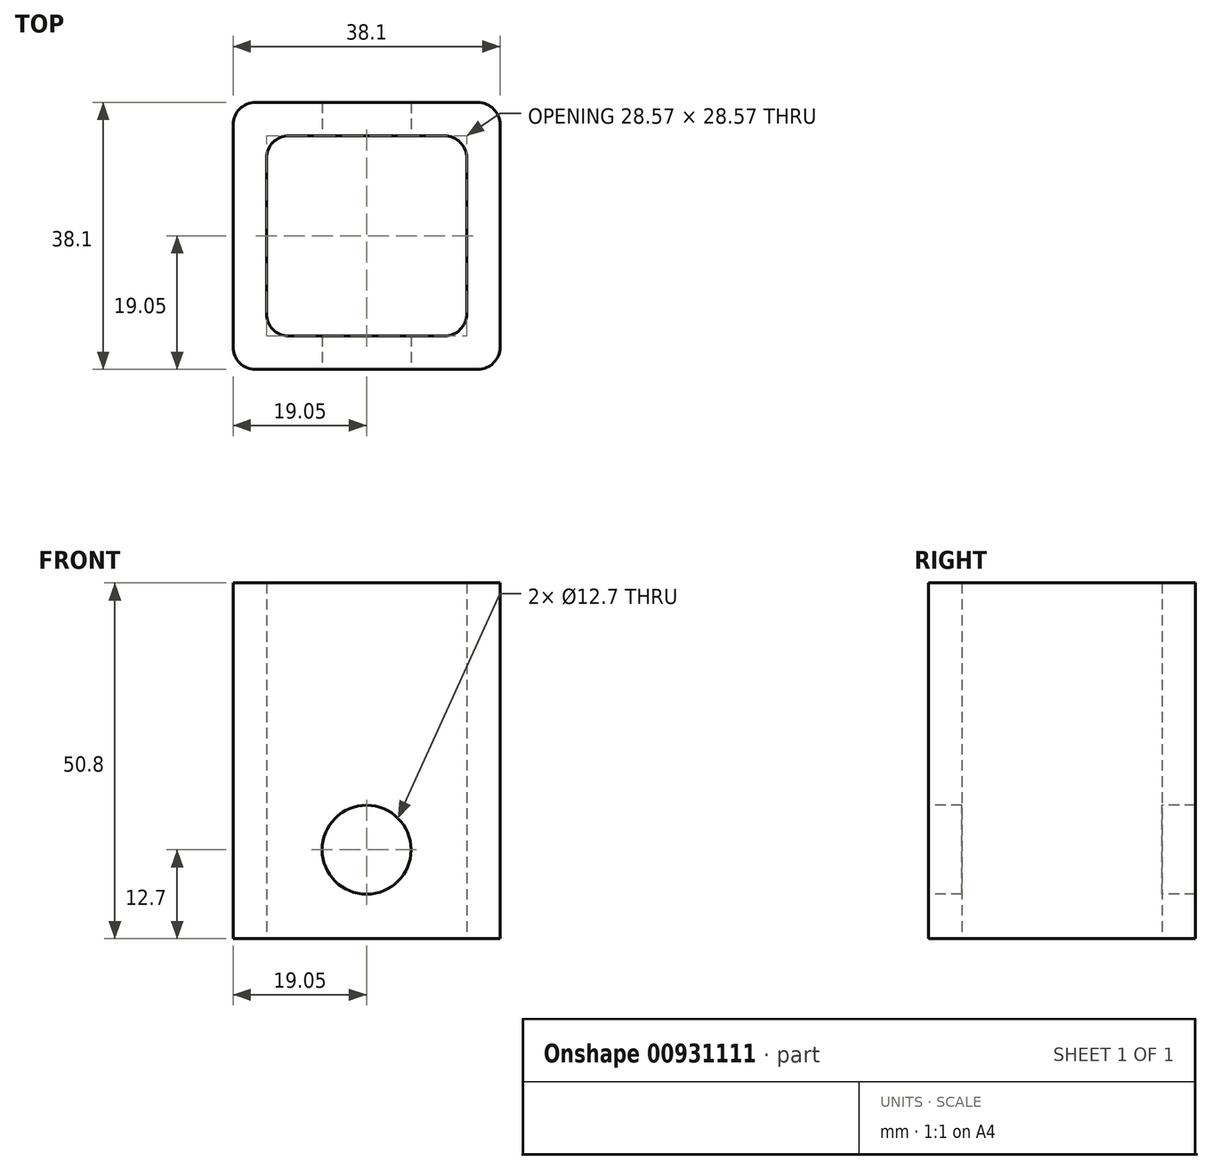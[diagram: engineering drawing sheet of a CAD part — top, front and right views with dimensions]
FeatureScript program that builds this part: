
annotation { "Feature Type Name" : "Feature", "Feature Type Description" : "" }
export const myFeature = defineFeature(function(context is Context, id is Id, definition is map)
    precondition{}
    {
        {
            var Q0;
            Q0=qCreatedBy(makeId("Top.planeOp"),FACE);
            var sketch = newSketch(context, id + "F0", { "sketchPlane" : qUnion([Q0])});
            skLineSegment(sketch, "E0.bottom", {"start": v(14.29, 14.29) * mm, "end": v(-14.29, 14.29) * mm});
            skLineSegment(sketch, "E0.top", {"start": v(14.29, -14.29) * mm, "end": v(-14.29, -14.29) * mm});
            skLineSegment(sketch, "E0.left", {"start": v(14.29, 14.29) * mm, "end": v(14.29, -14.29) * mm});
            skLineSegment(sketch, "E0.right", {"start": v(-14.29, 14.29) * mm, "end": v(-14.29, -14.29) * mm});
            skPoint(sketch, "E0.middle", {"position": v(0, 0) * mm});
            skLineSegment(sketch, "E1.bottom", {"start": v(19.05, 19.05) * mm, "end": v(-19.05, 19.05) * mm});
            skLineSegment(sketch, "E1.top", {"start": v(19.05, -19.05) * mm, "end": v(-19.05, -19.05) * mm});
            skLineSegment(sketch, "E1.left", {"start": v(19.05, 19.05) * mm, "end": v(19.05, -19.05) * mm});
            skLineSegment(sketch, "E1.right", {"start": v(-19.05, 19.05) * mm, "end": v(-19.05, -19.05) * mm});
            skSolve(sketch);
        }
        {
            var Q0;
            Q0 = qSketchRegion(id + "F0", true);
            extrude(context, id + "F1", {"entities" : qUnion([Q0]), "endBound" : BoundingType.SYMMETRIC, "depth" : 50.8 * mm, "offsetDistance" : 25.4 * mm});
        }
        {
            var Q0;
            Q0=makeQuery(id+"F1.opExtrude","SWEPT_EDGE",EDGE,{"disambiguationData":[OSD([sQuery(id+"F0.wireOp",EDGE,"E1.top"),sQuery(id+"F0.wireOp",EDGE,"E1.left")])]});
            var Q1;
            Q1=makeQuery(id+"F1.opExtrude","SWEPT_EDGE",EDGE,{"disambiguationData":[OSD([sQuery(id+"F0.wireOp",EDGE,"E1.top"),sQuery(id+"F0.wireOp",EDGE,"E1.right")])]});
            var Q2;
            Q2=makeQuery(id+"F1.opExtrude","SWEPT_EDGE",EDGE,{"disambiguationData":[OSD([sQuery(id+"F0.wireOp",EDGE,"E0.bottom"),sQuery(id+"F0.wireOp",EDGE,"E0.right")])]});
            var Q3;
            Q3=makeQuery(id+"F1.opExtrude","SWEPT_EDGE",EDGE,{"disambiguationData":[OSD([sQuery(id+"F0.wireOp",EDGE,"E0.bottom"),sQuery(id+"F0.wireOp",EDGE,"E0.left")])]});
            var Q4;
            Q4=makeQuery(id+"F1.opExtrude","SWEPT_EDGE",EDGE,{"disambiguationData":[OSD([sQuery(id+"F0.wireOp",EDGE,"E1.bottom"),sQuery(id+"F0.wireOp",EDGE,"E1.right")])]});
            var Q5;
            Q5=makeQuery(id+"F1.opExtrude","SWEPT_EDGE",EDGE,{"disambiguationData":[OSD([sQuery(id+"F0.wireOp",EDGE,"E1.bottom"),sQuery(id+"F0.wireOp",EDGE,"E1.left")])]});
            var Q6;
            Q6=makeQuery(id+"F1.opExtrude","SWEPT_EDGE",EDGE,{"disambiguationData":[OSD([sQuery(id+"F0.wireOp",EDGE,"E0.top"),sQuery(id+"F0.wireOp",EDGE,"E0.right")])]});
            var Q7;
            Q7=makeQuery(id+"F1.opExtrude","SWEPT_EDGE",EDGE,{"disambiguationData":[OSD([sQuery(id+"F0.wireOp",EDGE,"E0.top"),sQuery(id+"F0.wireOp",EDGE,"E0.left")])]});
            fillet(context, id + "F2", {"entities" : qUnion([Q0, Q1, Q2, Q3, Q4, Q5, Q6, Q7]), "radius" : 3.17 * mm, "tangentPropagation" : true, "allowEdgeOverflow" : false});
        }
        {
            var Q0;
            Q0=makeQuery(id+"F1.opExtrude","SWEPT_FACE",FACE,{"disambiguationData":[OSD([sQuery(id+"F0.wireOp",EDGE,"E1.top")])]});
            var sketch = newSketch(context, id + "F3", { "sketchPlane" : qUnion([Q0])});
            skCircle(sketch, "E2", {"center": v(0, -12.7) * mm, "radius": 6.35 * mm});
            skSolve(sketch);
        }
        {
            var Q0;
            Q0 = qSketchRegion(id + "F3", true);
            var Q1;
            Q1=makeQuery(id+"F1.opExtrude","SWEPT_FACE",FACE,{"disambiguationData":[OSD([sQuery(id+"F0.wireOp",EDGE,"E1.bottom")])]});
            extrude(context, id + "F4", {"entities" : qUnion([Q0]), "operationType" : NewBodyOperationType.REMOVE, "endBound" : BoundingType.UP_TO_SURFACE, "oppositeDirection" : true, "depth" : 25.4 * mm, "endBoundEntityFace" : qUnion([Q1]), "offsetDistance" : 25.4 * mm});
        }
    });
